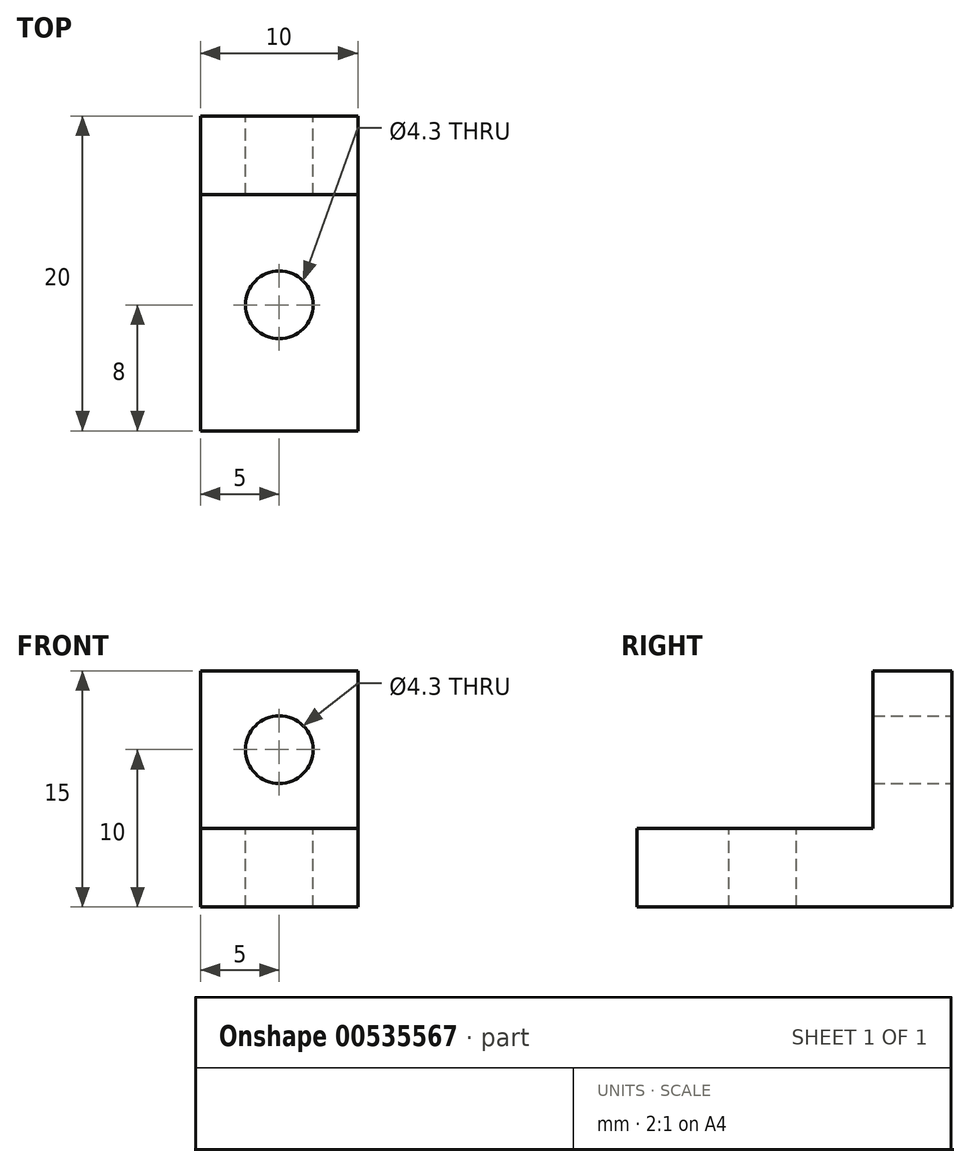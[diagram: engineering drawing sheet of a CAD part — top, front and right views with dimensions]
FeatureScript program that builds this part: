
annotation { "Feature Type Name" : "Feature", "Feature Type Description" : "" }
export const myFeature = defineFeature(function(context is Context, id is Id, definition is map)
    precondition{}
    {
        {
            var Q0;
            Q0=qCreatedBy(makeId("Front.planeOp"),FACE);
            var sketch = newSketch(context, id + "F0", { "sketchPlane" : qUnion([Q0])});
            skLineSegment(sketch, "E0.bottom", {"start": v(-5, 2.5) * mm, "end": v(5, 2.5) * mm});
            skLineSegment(sketch, "E0.top", {"start": v(-5, -2.5) * mm, "end": v(5, -2.5) * mm});
            skLineSegment(sketch, "E0.left", {"start": v(-5, 2.5) * mm, "end": v(-5, -2.5) * mm});
            skLineSegment(sketch, "E0.right", {"start": v(5, 2.5) * mm, "end": v(5, -2.5) * mm});
            skPoint(sketch, "E0.middle", {"position": v(0, 0) * mm});
            skSolve(sketch);
        }
        {
            var Q0;
            Q0 = qSketchRegion(id + "F0", true);
            extrude(context, id + "F1", {"entities" : qUnion([Q0]), "depth" : 20 * mm, "offsetDistance" : 25 * mm});
        }
        {
            var Q0;
            Q0=qCreatedBy(makeId("Right.planeOp"),FACE);
            var sketch = newSketch(context, id + "F2", { "sketchPlane" : qUnion([Q0])});
            skLineSegment(sketch, "E1.bottom", {"start": v(0, 2.5) * mm, "end": v(-5, 2.5) * mm});
            skLineSegment(sketch, "E1.top", {"start": v(0, 12.5) * mm, "end": v(-5, 12.5) * mm});
            skLineSegment(sketch, "E1.left", {"start": v(0, 2.5) * mm, "end": v(0, 12.5) * mm});
            skLineSegment(sketch, "E1.right", {"start": v(-5, 2.5) * mm, "end": v(-5, 12.5) * mm});
            skPoint(sketch, "E1.middle", {"position": v(-2.5, 7.5) * mm});
            skSolve(sketch);
        }
        {
            var Q0;
            Q0 = qSketchRegion(id + "F2", true);
            extrude(context, id + "F3", {"entities" : qUnion([Q0]), "operationType" : NewBodyOperationType.ADD, "depth" : 10 * mm, "offsetDistance" : 25 * mm, "symmetric" : true});
        }
        {
            var Q0;
            Q0=qCreatedBy(makeId("Top.planeOp"),FACE);
            var sketch = newSketch(context, id + "F4", { "sketchPlane" : qUnion([Q0])});
            skCircle(sketch, "E2", {"center": v(0, -12) * mm, "radius": 2.15 * mm});
            skSolve(sketch);
        }
        {
            var Q0;
            Q0 = qSketchRegion(id + "F4", true);
            extrude(context, id + "F5", {"entities" : qUnion([Q0]), "operationType" : NewBodyOperationType.REMOVE, "oppositeDirection" : true, "depth" : 25 * mm, "offsetDistance" : 25 * mm, "symmetric" : true});
        }
        {
            var Q0;
            Q0=qCreatedBy(makeId("Front.planeOp"),FACE);
            var sketch = newSketch(context, id + "F6", { "sketchPlane" : qUnion([Q0])});
            skCircle(sketch, "E3", {"center": v(0, 7.5) * mm, "radius": 2.15 * mm});
            skSolve(sketch);
        }
        {
            var Q0;
            Q0 = qSketchRegion(id + "F6", true);
            extrude(context, id + "F7", {"entities" : qUnion([Q0]), "operationType" : NewBodyOperationType.REMOVE, "depth" : 5.1 * mm, "offsetDistance" : 25 * mm});
        }
    });
